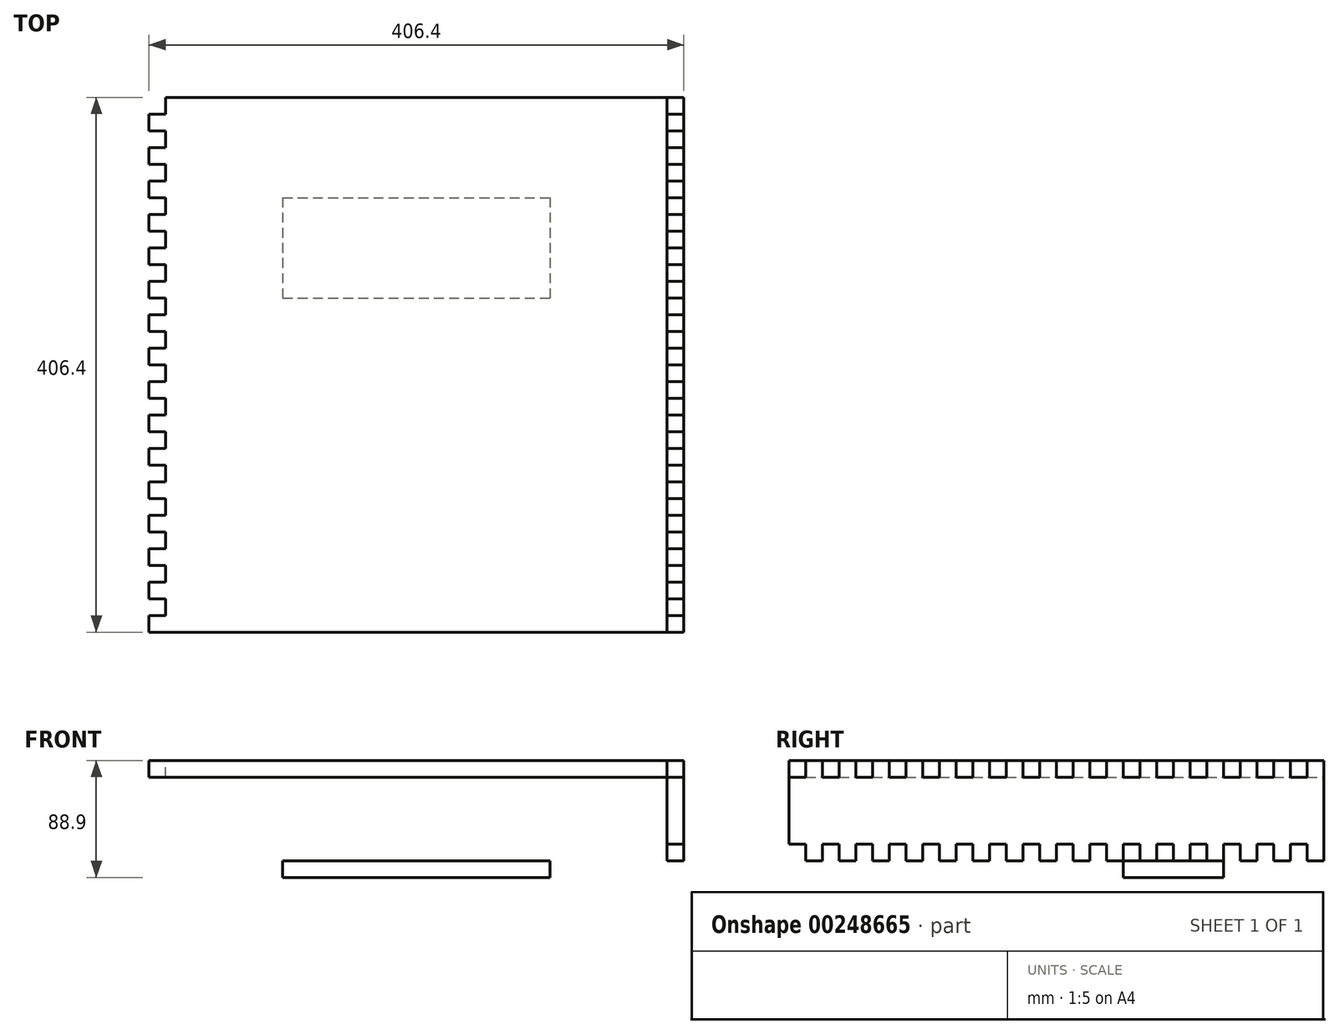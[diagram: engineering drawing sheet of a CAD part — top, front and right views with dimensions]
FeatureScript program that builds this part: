
annotation { "Feature Type Name" : "Feature", "Feature Type Description" : "" }
export const myFeature = defineFeature(function(context is Context, id is Id, definition is map)
    precondition{}
    {
        {
            var Q0;
            Q0=qCreatedBy(makeId("Top.planeOp"),FACE);
            var sketch = newSketch(context, id + "F0", { "sketchPlane" : qUnion([Q0])});
            skLineSegment(sketch, "E0.bottom", {"start": v(203.2, 203.2) * mm, "end": v(-203.2, 203.2) * mm});
            skLineSegment(sketch, "E0.top", {"start": v(203.2, -203.2) * mm, "end": v(-203.2, -203.2) * mm});
            skLineSegment(sketch, "E0.left", {"start": v(203.2, 203.2) * mm, "end": v(203.2, -203.2) * mm});
            skLineSegment(sketch, "E0.right", {"start": v(-203.2, 203.2) * mm, "end": v(-203.2, -203.2) * mm});
            skPoint(sketch, "E0.middle", {"position": v(0, 0) * mm});
            skSolve(sketch);
        }
        {
            var Q0;
            Q0 = qSketchRegion(id + "F0", true);
            extrude(context, id + "F1", {"entities" : qUnion([Q0]), "depth" : 12.7 * mm});
        }
        {
            var Q0;
            Q0=makeQuery(id+"F1.opExtrude","CAP_FACE",FACE,{"disambiguationData":[OSD([sQuery(id+"F0.wireOp",EDGE,"E0.bottom"),sQuery(id+"F0.wireOp",EDGE,"E0.top"),sQuery(id+"F0.wireOp",EDGE,"E0.left"),sQuery(id+"F0.wireOp",EDGE,"E0.right")])],"isStart":false});
            var sketch = newSketch(context, id + "F2", { "sketchPlane" : qUnion([Q0])});
            skLineSegment(sketch, "E1.bottom", {"start": v(-203.2, 203.2) * mm, "end": v(-190.5, 203.2) * mm});
            skLineSegment(sketch, "E1.top", {"start": v(-203.2, 190.5) * mm, "end": v(-190.5, 190.5) * mm});
            skLineSegment(sketch, "E1.left", {"start": v(-203.2, 203.2) * mm, "end": v(-203.2, 190.5) * mm});
            skLineSegment(sketch, "E1.right", {"start": v(-190.5, 203.2) * mm, "end": v(-190.5, 190.5) * mm});
            skLineSegment(sketch, "E2.0.1.0", {"start": v(-203.2, 177.8) * mm, "end": v(-203.2, 165.1) * mm});
            skLineSegment(sketch, "E2.0.1.1", {"start": v(-203.2, 165.1) * mm, "end": v(-190.5, 165.1) * mm});
            skLineSegment(sketch, "E2.0.1.2", {"start": v(-190.5, 177.8) * mm, "end": v(-190.5, 165.1) * mm});
            skLineSegment(sketch, "E2.0.1.3", {"start": v(-203.2, 177.8) * mm, "end": v(-190.5, 177.8) * mm});
            skLineSegment(sketch, "E2.0.2.0", {"start": v(-203.2, 152.4) * mm, "end": v(-203.2, 139.7) * mm});
            skLineSegment(sketch, "E2.0.2.1", {"start": v(-203.2, 139.7) * mm, "end": v(-190.5, 139.7) * mm});
            skLineSegment(sketch, "E2.0.2.2", {"start": v(-190.5, 152.4) * mm, "end": v(-190.5, 139.7) * mm});
            skLineSegment(sketch, "E2.0.2.3", {"start": v(-203.2, 152.4) * mm, "end": v(-190.5, 152.4) * mm});
            skLineSegment(sketch, "E2.0.3.0", {"start": v(-203.2, 127) * mm, "end": v(-203.2, 114.3) * mm});
            skLineSegment(sketch, "E2.0.3.1", {"start": v(-203.2, 114.3) * mm, "end": v(-190.5, 114.3) * mm});
            skLineSegment(sketch, "E2.0.3.2", {"start": v(-190.5, 127) * mm, "end": v(-190.5, 114.3) * mm});
            skLineSegment(sketch, "E2.0.3.3", {"start": v(-203.2, 127) * mm, "end": v(-190.5, 127) * mm});
            skLineSegment(sketch, "E2.0.4.0", {"start": v(-203.2, 101.6) * mm, "end": v(-203.2, 88.9) * mm});
            skLineSegment(sketch, "E2.0.4.1", {"start": v(-203.2, 88.9) * mm, "end": v(-190.5, 88.9) * mm});
            skLineSegment(sketch, "E2.0.4.2", {"start": v(-190.5, 101.6) * mm, "end": v(-190.5, 88.9) * mm});
            skLineSegment(sketch, "E2.0.4.3", {"start": v(-203.2, 101.6) * mm, "end": v(-190.5, 101.6) * mm});
            skLineSegment(sketch, "E2.0.5.0", {"start": v(-203.2, 76.2) * mm, "end": v(-203.2, 63.5) * mm});
            skLineSegment(sketch, "E2.0.5.1", {"start": v(-203.2, 63.5) * mm, "end": v(-190.5, 63.5) * mm});
            skLineSegment(sketch, "E2.0.5.2", {"start": v(-190.5, 76.2) * mm, "end": v(-190.5, 63.5) * mm});
            skLineSegment(sketch, "E2.0.5.3", {"start": v(-203.2, 76.2) * mm, "end": v(-190.5, 76.2) * mm});
            skLineSegment(sketch, "E2.0.6.0", {"start": v(-203.2, 50.8) * mm, "end": v(-203.2, 38.1) * mm});
            skLineSegment(sketch, "E2.0.6.1", {"start": v(-203.2, 38.1) * mm, "end": v(-190.5, 38.1) * mm});
            skLineSegment(sketch, "E2.0.6.2", {"start": v(-190.5, 50.8) * mm, "end": v(-190.5, 38.1) * mm});
            skLineSegment(sketch, "E2.0.6.3", {"start": v(-203.2, 50.8) * mm, "end": v(-190.5, 50.8) * mm});
            skLineSegment(sketch, "E2.0.7.0", {"start": v(-203.2, 25.4) * mm, "end": v(-203.2, 12.7) * mm});
            skLineSegment(sketch, "E2.0.7.1", {"start": v(-203.2, 12.7) * mm, "end": v(-190.5, 12.7) * mm});
            skLineSegment(sketch, "E2.0.7.2", {"start": v(-190.5, 25.4) * mm, "end": v(-190.5, 12.7) * mm});
            skLineSegment(sketch, "E2.0.7.3", {"start": v(-203.2, 25.4) * mm, "end": v(-190.5, 25.4) * mm});
            skLineSegment(sketch, "E2.0.8.0", {"start": v(-203.2, 0) * mm, "end": v(-203.2, -12.7) * mm});
            skLineSegment(sketch, "E2.0.8.1", {"start": v(-203.2, -12.7) * mm, "end": v(-190.5, -12.7) * mm});
            skLineSegment(sketch, "E2.0.8.2", {"start": v(-190.5, 0) * mm, "end": v(-190.5, -12.7) * mm});
            skLineSegment(sketch, "E2.0.8.3", {"start": v(-203.2, 0) * mm, "end": v(-190.5, 0) * mm});
            skLineSegment(sketch, "E2.0.9.0", {"start": v(-203.2, -25.4) * mm, "end": v(-203.2, -38.1) * mm});
            skLineSegment(sketch, "E2.0.9.1", {"start": v(-203.2, -38.1) * mm, "end": v(-190.5, -38.1) * mm});
            skLineSegment(sketch, "E2.0.9.2", {"start": v(-190.5, -25.4) * mm, "end": v(-190.5, -38.1) * mm});
            skLineSegment(sketch, "E2.0.9.3", {"start": v(-203.2, -25.4) * mm, "end": v(-190.5, -25.4) * mm});
            skLineSegment(sketch, "E2.0.10.0", {"start": v(-203.2, -50.8) * mm, "end": v(-203.2, -63.5) * mm});
            skLineSegment(sketch, "E2.0.10.1", {"start": v(-203.2, -63.5) * mm, "end": v(-190.5, -63.5) * mm});
            skLineSegment(sketch, "E2.0.10.2", {"start": v(-190.5, -50.8) * mm, "end": v(-190.5, -63.5) * mm});
            skLineSegment(sketch, "E2.0.10.3", {"start": v(-203.2, -50.8) * mm, "end": v(-190.5, -50.8) * mm});
            skLineSegment(sketch, "E2.0.11.0", {"start": v(-203.2, -76.2) * mm, "end": v(-203.2, -88.9) * mm});
            skLineSegment(sketch, "E2.0.11.1", {"start": v(-203.2, -88.9) * mm, "end": v(-190.5, -88.9) * mm});
            skLineSegment(sketch, "E2.0.11.2", {"start": v(-190.5, -76.2) * mm, "end": v(-190.5, -88.9) * mm});
            skLineSegment(sketch, "E2.0.11.3", {"start": v(-203.2, -76.2) * mm, "end": v(-190.5, -76.2) * mm});
            skLineSegment(sketch, "E2.0.12.0", {"start": v(-203.2, -101.6) * mm, "end": v(-203.2, -114.3) * mm});
            skLineSegment(sketch, "E2.0.12.1", {"start": v(-203.2, -114.3) * mm, "end": v(-190.5, -114.3) * mm});
            skLineSegment(sketch, "E2.0.12.2", {"start": v(-190.5, -101.6) * mm, "end": v(-190.5, -114.3) * mm});
            skLineSegment(sketch, "E2.0.12.3", {"start": v(-203.2, -101.6) * mm, "end": v(-190.5, -101.6) * mm});
            skLineSegment(sketch, "E2.0.13.0", {"start": v(-203.2, -127) * mm, "end": v(-203.2, -139.7) * mm});
            skLineSegment(sketch, "E2.0.13.1", {"start": v(-203.2, -139.7) * mm, "end": v(-190.5, -139.7) * mm});
            skLineSegment(sketch, "E2.0.13.2", {"start": v(-190.5, -127) * mm, "end": v(-190.5, -139.7) * mm});
            skLineSegment(sketch, "E2.0.13.3", {"start": v(-203.2, -127) * mm, "end": v(-190.5, -127) * mm});
            skLineSegment(sketch, "E2.0.14.0", {"start": v(-203.2, -152.4) * mm, "end": v(-203.2, -165.1) * mm});
            skLineSegment(sketch, "E2.0.14.1", {"start": v(-203.2, -165.1) * mm, "end": v(-190.5, -165.1) * mm});
            skLineSegment(sketch, "E2.0.14.2", {"start": v(-190.5, -152.4) * mm, "end": v(-190.5, -165.1) * mm});
            skLineSegment(sketch, "E2.0.14.3", {"start": v(-203.2, -152.4) * mm, "end": v(-190.5, -152.4) * mm});
            skLineSegment(sketch, "E2.0.15.0", {"start": v(-203.2, -177.8) * mm, "end": v(-203.2, -190.5) * mm});
            skLineSegment(sketch, "E2.0.15.1", {"start": v(-203.2, -190.5) * mm, "end": v(-190.5, -190.5) * mm});
            skLineSegment(sketch, "E2.0.15.2", {"start": v(-190.5, -177.8) * mm, "end": v(-190.5, -190.5) * mm});
            skLineSegment(sketch, "E2.0.15.3", {"start": v(-203.2, -177.8) * mm, "end": v(-190.5, -177.8) * mm});
            skLineSegment(sketch, "E2.direction1", {"start": v(-203.2, 190.5) * mm, "end": v(190.5, 190.5) * mm, "construction": true});
            skLineSegment(sketch, "E2.direction2", {"start": v(-203.2, 190.5) * mm, "end": v(-203.2, 165.1) * mm, "construction": true});
            skLineSegment(sketch, "E3.0.1.0", {"start": v(190.5, 203.2) * mm, "end": v(190.5, 190.5) * mm});
            skLineSegment(sketch, "E3.3.1.0", {"start": v(190.5, 190.5) * mm, "end": v(203.2, 190.5) * mm});
            skLineSegment(sketch, "E3.6.1.0", {"start": v(203.2, 203.2) * mm, "end": v(203.2, 190.5) * mm});
            skLineSegment(sketch, "E3.9.1.0", {"start": v(190.5, 203.2) * mm, "end": v(203.2, 203.2) * mm});
            skLineSegment(sketch, "E3.0.1.1", {"start": v(190.5, 177.8) * mm, "end": v(190.5, 165.1) * mm});
            skLineSegment(sketch, "E3.3.1.1", {"start": v(190.5, 165.1) * mm, "end": v(203.2, 165.1) * mm});
            skLineSegment(sketch, "E3.6.1.1", {"start": v(203.2, 177.8) * mm, "end": v(203.2, 165.1) * mm});
            skLineSegment(sketch, "E3.9.1.1", {"start": v(190.5, 177.8) * mm, "end": v(203.2, 177.8) * mm});
            skLineSegment(sketch, "E3.0.1.2", {"start": v(190.5, 152.4) * mm, "end": v(190.5, 139.7) * mm});
            skLineSegment(sketch, "E3.3.1.2", {"start": v(190.5, 139.7) * mm, "end": v(203.2, 139.7) * mm});
            skLineSegment(sketch, "E3.6.1.2", {"start": v(203.2, 152.4) * mm, "end": v(203.2, 139.7) * mm});
            skLineSegment(sketch, "E3.9.1.2", {"start": v(190.5, 152.4) * mm, "end": v(203.2, 152.4) * mm});
            skLineSegment(sketch, "E3.0.1.3", {"start": v(190.5, 127) * mm, "end": v(190.5, 114.3) * mm});
            skLineSegment(sketch, "E3.3.1.3", {"start": v(190.5, 114.3) * mm, "end": v(203.2, 114.3) * mm});
            skLineSegment(sketch, "E3.6.1.3", {"start": v(203.2, 127) * mm, "end": v(203.2, 114.3) * mm});
            skLineSegment(sketch, "E3.9.1.3", {"start": v(190.5, 127) * mm, "end": v(203.2, 127) * mm});
            skLineSegment(sketch, "E3.0.1.4", {"start": v(190.5, 101.6) * mm, "end": v(190.5, 88.9) * mm});
            skLineSegment(sketch, "E3.3.1.4", {"start": v(190.5, 88.9) * mm, "end": v(203.2, 88.9) * mm});
            skLineSegment(sketch, "E3.6.1.4", {"start": v(203.2, 101.6) * mm, "end": v(203.2, 88.9) * mm});
            skLineSegment(sketch, "E3.9.1.4", {"start": v(190.5, 101.6) * mm, "end": v(203.2, 101.6) * mm});
            skLineSegment(sketch, "E3.0.1.5", {"start": v(190.5, 76.2) * mm, "end": v(190.5, 63.5) * mm});
            skLineSegment(sketch, "E3.3.1.5", {"start": v(190.5, 63.5) * mm, "end": v(203.2, 63.5) * mm});
            skLineSegment(sketch, "E3.6.1.5", {"start": v(203.2, 76.2) * mm, "end": v(203.2, 63.5) * mm});
            skLineSegment(sketch, "E3.9.1.5", {"start": v(190.5, 76.2) * mm, "end": v(203.2, 76.2) * mm});
            skLineSegment(sketch, "E3.0.1.6", {"start": v(190.5, 50.8) * mm, "end": v(190.5, 38.1) * mm});
            skLineSegment(sketch, "E3.3.1.6", {"start": v(190.5, 38.1) * mm, "end": v(203.2, 38.1) * mm});
            skLineSegment(sketch, "E3.6.1.6", {"start": v(203.2, 50.8) * mm, "end": v(203.2, 38.1) * mm});
            skLineSegment(sketch, "E3.9.1.6", {"start": v(190.5, 50.8) * mm, "end": v(203.2, 50.8) * mm});
            skLineSegment(sketch, "E3.0.1.7", {"start": v(190.5, 25.4) * mm, "end": v(190.5, 12.7) * mm});
            skLineSegment(sketch, "E3.3.1.7", {"start": v(190.5, 12.7) * mm, "end": v(203.2, 12.7) * mm});
            skLineSegment(sketch, "E3.6.1.7", {"start": v(203.2, 25.4) * mm, "end": v(203.2, 12.7) * mm});
            skLineSegment(sketch, "E3.9.1.7", {"start": v(190.5, 25.4) * mm, "end": v(203.2, 25.4) * mm});
            skLineSegment(sketch, "E3.0.1.8", {"start": v(190.5, 0) * mm, "end": v(190.5, -12.7) * mm});
            skLineSegment(sketch, "E3.3.1.8", {"start": v(190.5, -12.7) * mm, "end": v(203.2, -12.7) * mm});
            skLineSegment(sketch, "E3.6.1.8", {"start": v(203.2, 0) * mm, "end": v(203.2, -12.7) * mm});
            skLineSegment(sketch, "E3.9.1.8", {"start": v(190.5, 0) * mm, "end": v(203.2, 0) * mm});
            skLineSegment(sketch, "E3.0.1.9", {"start": v(190.5, -25.4) * mm, "end": v(190.5, -38.1) * mm});
            skLineSegment(sketch, "E3.3.1.9", {"start": v(190.5, -38.1) * mm, "end": v(203.2, -38.1) * mm});
            skLineSegment(sketch, "E3.6.1.9", {"start": v(203.2, -25.4) * mm, "end": v(203.2, -38.1) * mm});
            skLineSegment(sketch, "E3.9.1.9", {"start": v(190.5, -25.4) * mm, "end": v(203.2, -25.4) * mm});
            skLineSegment(sketch, "E3.0.1.10", {"start": v(190.5, -50.8) * mm, "end": v(190.5, -63.5) * mm});
            skLineSegment(sketch, "E3.3.1.10", {"start": v(190.5, -63.5) * mm, "end": v(203.2, -63.5) * mm});
            skLineSegment(sketch, "E3.6.1.10", {"start": v(203.2, -50.8) * mm, "end": v(203.2, -63.5) * mm});
            skLineSegment(sketch, "E3.9.1.10", {"start": v(190.5, -50.8) * mm, "end": v(203.2, -50.8) * mm});
            skLineSegment(sketch, "E3.0.1.11", {"start": v(190.5, -76.2) * mm, "end": v(190.5, -88.9) * mm});
            skLineSegment(sketch, "E3.3.1.11", {"start": v(190.5, -88.9) * mm, "end": v(203.2, -88.9) * mm});
            skLineSegment(sketch, "E3.6.1.11", {"start": v(203.2, -76.2) * mm, "end": v(203.2, -88.9) * mm});
            skLineSegment(sketch, "E3.9.1.11", {"start": v(190.5, -76.2) * mm, "end": v(203.2, -76.2) * mm});
            skLineSegment(sketch, "E3.0.1.12", {"start": v(190.5, -101.6) * mm, "end": v(190.5, -114.3) * mm});
            skLineSegment(sketch, "E3.3.1.12", {"start": v(190.5, -114.3) * mm, "end": v(203.2, -114.3) * mm});
            skLineSegment(sketch, "E3.6.1.12", {"start": v(203.2, -101.6) * mm, "end": v(203.2, -114.3) * mm});
            skLineSegment(sketch, "E3.9.1.12", {"start": v(190.5, -101.6) * mm, "end": v(203.2, -101.6) * mm});
            skLineSegment(sketch, "E3.0.1.13", {"start": v(190.5, -127) * mm, "end": v(190.5, -139.7) * mm});
            skLineSegment(sketch, "E3.3.1.13", {"start": v(190.5, -139.7) * mm, "end": v(203.2, -139.7) * mm});
            skLineSegment(sketch, "E3.6.1.13", {"start": v(203.2, -127) * mm, "end": v(203.2, -139.7) * mm});
            skLineSegment(sketch, "E3.9.1.13", {"start": v(190.5, -127) * mm, "end": v(203.2, -127) * mm});
            skLineSegment(sketch, "E3.0.1.14", {"start": v(190.5, -152.4) * mm, "end": v(190.5, -165.1) * mm});
            skLineSegment(sketch, "E3.3.1.14", {"start": v(190.5, -165.1) * mm, "end": v(203.2, -165.1) * mm});
            skLineSegment(sketch, "E3.6.1.14", {"start": v(203.2, -152.4) * mm, "end": v(203.2, -165.1) * mm});
            skLineSegment(sketch, "E3.9.1.14", {"start": v(190.5, -152.4) * mm, "end": v(203.2, -152.4) * mm});
            skLineSegment(sketch, "E3.0.1.15", {"start": v(190.5, -177.8) * mm, "end": v(190.5, -190.5) * mm});
            skLineSegment(sketch, "E3.3.1.15", {"start": v(190.5, -190.5) * mm, "end": v(203.2, -190.5) * mm});
            skLineSegment(sketch, "E3.6.1.15", {"start": v(203.2, -177.8) * mm, "end": v(203.2, -190.5) * mm});
            skLineSegment(sketch, "E3.9.1.15", {"start": v(190.5, -177.8) * mm, "end": v(203.2, -177.8) * mm});
            skSolve(sketch);
        }
        {
            var Q0;
            Q0 = qSketchRegion(id + "F2", true);
            extrude(context, id + "F3", {"entities" : qUnion([Q0]), "operationType" : NewBodyOperationType.REMOVE, "endBound" : BoundingType.UP_TO_NEXT, "oppositeDirection" : true, "depth" : 25.4 * mm});
        }
        {
            var Q0;
            {var subQ1=sQuery(id+"F0.wireOp",EDGE,"E0.left");var subQ2=sQuery(id+"F0.wireOp",EDGE,"E0.top");Q0=makeQuery(id+"F3.boolean.opBoolean","SPLIT",FACE,{"disambiguationData":[TD([makeQuery(id+"F1.opExtrude","SWEPT_FACE",FACE,{"disambiguationData":[OSD([subQ2])]})])],"derivedFrom":makeQuery(id+"F1.opExtrude","SWEPT_FACE",FACE,{"disambiguationData":[OSD([subQ1])]})});}
            var sketch = newSketch(context, id + "F4", { "sketchPlane" : qUnion([Q0])});
            skLineSegment(sketch, "E4.bottom", {"start": v(-203.2, 12.7) * mm, "end": v(203.2, 12.7) * mm});
            skLineSegment(sketch, "E4.top", {"start": v(-203.2, -63.5) * mm, "end": v(203.2, -63.5) * mm});
            skLineSegment(sketch, "E4.left", {"start": v(-203.2, 12.7) * mm, "end": v(-203.2, -63.5) * mm});
            skLineSegment(sketch, "E4.right", {"start": v(203.2, 12.7) * mm, "end": v(203.2, -63.5) * mm});
            skSolve(sketch);
        }
        {
            var Q0;
            Q0 = qSketchRegion(id + "F4", true);
            extrude(context, id + "F5", {"entities" : qUnion([Q0]), "oppositeDirection" : true, "depth" : 12.7 * mm});
        }
        {
            var Q0;
            Q0=makeQuery(id+"F5.opExtrude","CAP_FACE",FACE,{"disambiguationData":[OSD([sQuery(id+"F4.wireOp",EDGE,"E4.bottom"),sQuery(id+"F4.wireOp",EDGE,"E4.top"),sQuery(id+"F4.wireOp",EDGE,"E4.left"),sQuery(id+"F4.wireOp",EDGE,"E4.right")])],"isStart":true});
            var sketch = newSketch(context, id + "F6", { "sketchPlane" : qUnion([Q0])});
            skLineSegment(sketch, "E5.0", {"start": v(-203.2, 12.7) * mm, "end": v(-190.5, 12.7) * mm});
            skLineSegment(sketch, "E5.1", {"start": v(-203.2, 12.7) * mm, "end": v(-203.2, 0) * mm});
            skLineSegment(sketch, "E5.2", {"start": v(-190.5, 0) * mm, "end": v(-190.5, 12.7) * mm});
            skLineSegment(sketch, "E5.3", {"start": v(-190.5, 0) * mm, "end": v(-203.2, 0) * mm});
            skPoint(sketch, "E6.orphan", {"position": v(203.2, 12.7) * mm});
            skPoint(sketch, "E7.orphan", {"position": v(-203.2, -63.5) * mm});
            skLineSegment(sketch, "E8.0.1.0", {"start": v(-203.2, -50.8) * mm, "end": v(-190.5, -50.8) * mm});
            skLineSegment(sketch, "E8.0.1.1", {"start": v(-190.5, -63.5) * mm, "end": v(-190.5, -50.8) * mm});
            skLineSegment(sketch, "E8.0.1.2", {"start": v(-190.5, -63.5) * mm, "end": v(-203.2, -63.5) * mm});
            skLineSegment(sketch, "E8.0.1.3", {"start": v(-203.2, -50.8) * mm, "end": v(-203.2, -63.5) * mm});
            skLineSegment(sketch, "E8.1.0.0", {"start": v(-177.8, 12.7) * mm, "end": v(-165.1, 12.7) * mm});
            skLineSegment(sketch, "E8.1.0.1", {"start": v(-165.1, 0) * mm, "end": v(-165.1, 12.7) * mm});
            skLineSegment(sketch, "E8.1.0.2", {"start": v(-165.1, 0) * mm, "end": v(-177.8, 0) * mm});
            skLineSegment(sketch, "E8.1.0.3", {"start": v(-177.8, 12.7) * mm, "end": v(-177.8, 0) * mm});
            skLineSegment(sketch, "E8.1.1.0", {"start": v(-177.8, -50.8) * mm, "end": v(-165.1, -50.8) * mm});
            skLineSegment(sketch, "E8.1.1.1", {"start": v(-165.1, -63.5) * mm, "end": v(-165.1, -50.8) * mm});
            skLineSegment(sketch, "E8.1.1.2", {"start": v(-165.1, -63.5) * mm, "end": v(-177.8, -63.5) * mm});
            skLineSegment(sketch, "E8.1.1.3", {"start": v(-177.8, -50.8) * mm, "end": v(-177.8, -63.5) * mm});
            skLineSegment(sketch, "E8.2.0.0", {"start": v(-152.4, 12.7) * mm, "end": v(-139.7, 12.7) * mm});
            skLineSegment(sketch, "E8.2.0.1", {"start": v(-139.7, 0) * mm, "end": v(-139.7, 12.7) * mm});
            skLineSegment(sketch, "E8.2.0.2", {"start": v(-139.7, 0) * mm, "end": v(-152.4, 0) * mm});
            skLineSegment(sketch, "E8.2.0.3", {"start": v(-152.4, 12.7) * mm, "end": v(-152.4, 0) * mm});
            skLineSegment(sketch, "E8.2.1.0", {"start": v(-152.4, -50.8) * mm, "end": v(-139.7, -50.8) * mm});
            skLineSegment(sketch, "E8.2.1.1", {"start": v(-139.7, -63.5) * mm, "end": v(-139.7, -50.8) * mm});
            skLineSegment(sketch, "E8.2.1.2", {"start": v(-139.7, -63.5) * mm, "end": v(-152.4, -63.5) * mm});
            skLineSegment(sketch, "E8.2.1.3", {"start": v(-152.4, -50.8) * mm, "end": v(-152.4, -63.5) * mm});
            skLineSegment(sketch, "E8.3.0.0", {"start": v(-127, 12.7) * mm, "end": v(-114.3, 12.7) * mm});
            skLineSegment(sketch, "E8.3.0.1", {"start": v(-114.3, 0) * mm, "end": v(-114.3, 12.7) * mm});
            skLineSegment(sketch, "E8.3.0.2", {"start": v(-114.3, 0) * mm, "end": v(-127, 0) * mm});
            skLineSegment(sketch, "E8.3.0.3", {"start": v(-127, 12.7) * mm, "end": v(-127, 0) * mm});
            skLineSegment(sketch, "E8.3.1.0", {"start": v(-127, -50.8) * mm, "end": v(-114.3, -50.8) * mm});
            skLineSegment(sketch, "E8.3.1.1", {"start": v(-114.3, -63.5) * mm, "end": v(-114.3, -50.8) * mm});
            skLineSegment(sketch, "E8.3.1.2", {"start": v(-114.3, -63.5) * mm, "end": v(-127, -63.5) * mm});
            skLineSegment(sketch, "E8.3.1.3", {"start": v(-127, -50.8) * mm, "end": v(-127, -63.5) * mm});
            skLineSegment(sketch, "E8.4.0.0", {"start": v(-101.6, 12.7) * mm, "end": v(-88.9, 12.7) * mm});
            skLineSegment(sketch, "E8.4.0.1", {"start": v(-88.9, 0) * mm, "end": v(-88.9, 12.7) * mm});
            skLineSegment(sketch, "E8.4.0.2", {"start": v(-88.9, 0) * mm, "end": v(-101.6, 0) * mm});
            skLineSegment(sketch, "E8.4.0.3", {"start": v(-101.6, 12.7) * mm, "end": v(-101.6, 0) * mm});
            skLineSegment(sketch, "E8.4.1.0", {"start": v(-101.6, -50.8) * mm, "end": v(-88.9, -50.8) * mm});
            skLineSegment(sketch, "E8.4.1.1", {"start": v(-88.9, -63.5) * mm, "end": v(-88.9, -50.8) * mm});
            skLineSegment(sketch, "E8.4.1.2", {"start": v(-88.9, -63.5) * mm, "end": v(-101.6, -63.5) * mm});
            skLineSegment(sketch, "E8.4.1.3", {"start": v(-101.6, -50.8) * mm, "end": v(-101.6, -63.5) * mm});
            skLineSegment(sketch, "E8.5.0.0", {"start": v(-76.2, 12.7) * mm, "end": v(-63.5, 12.7) * mm});
            skLineSegment(sketch, "E8.5.0.1", {"start": v(-63.5, 0) * mm, "end": v(-63.5, 12.7) * mm});
            skLineSegment(sketch, "E8.5.0.2", {"start": v(-63.5, 0) * mm, "end": v(-76.2, 0) * mm});
            skLineSegment(sketch, "E8.5.0.3", {"start": v(-76.2, 12.7) * mm, "end": v(-76.2, 0) * mm});
            skLineSegment(sketch, "E8.5.1.0", {"start": v(-76.2, -50.8) * mm, "end": v(-63.5, -50.8) * mm});
            skLineSegment(sketch, "E8.5.1.1", {"start": v(-63.5, -63.5) * mm, "end": v(-63.5, -50.8) * mm});
            skLineSegment(sketch, "E8.5.1.2", {"start": v(-63.5, -63.5) * mm, "end": v(-76.2, -63.5) * mm});
            skLineSegment(sketch, "E8.5.1.3", {"start": v(-76.2, -50.8) * mm, "end": v(-76.2, -63.5) * mm});
            skLineSegment(sketch, "E8.6.0.0", {"start": v(-50.8, 12.7) * mm, "end": v(-38.1, 12.7) * mm});
            skLineSegment(sketch, "E8.6.0.1", {"start": v(-38.1, 0) * mm, "end": v(-38.1, 12.7) * mm});
            skLineSegment(sketch, "E8.6.0.2", {"start": v(-38.1, 0) * mm, "end": v(-50.8, 0) * mm});
            skLineSegment(sketch, "E8.6.0.3", {"start": v(-50.8, 12.7) * mm, "end": v(-50.8, 0) * mm});
            skLineSegment(sketch, "E8.6.1.0", {"start": v(-50.8, -50.8) * mm, "end": v(-38.1, -50.8) * mm});
            skLineSegment(sketch, "E8.6.1.1", {"start": v(-38.1, -63.5) * mm, "end": v(-38.1, -50.8) * mm});
            skLineSegment(sketch, "E8.6.1.2", {"start": v(-38.1, -63.5) * mm, "end": v(-50.8, -63.5) * mm});
            skLineSegment(sketch, "E8.6.1.3", {"start": v(-50.8, -50.8) * mm, "end": v(-50.8, -63.5) * mm});
            skLineSegment(sketch, "E8.7.0.0", {"start": v(-25.4, 12.7) * mm, "end": v(-12.7, 12.7) * mm});
            skLineSegment(sketch, "E8.7.0.1", {"start": v(-12.7, 0) * mm, "end": v(-12.7, 12.7) * mm});
            skLineSegment(sketch, "E8.7.0.2", {"start": v(-12.7, 0) * mm, "end": v(-25.4, 0) * mm});
            skLineSegment(sketch, "E8.7.0.3", {"start": v(-25.4, 12.7) * mm, "end": v(-25.4, 0) * mm});
            skLineSegment(sketch, "E8.7.1.0", {"start": v(-25.4, -50.8) * mm, "end": v(-12.7, -50.8) * mm});
            skLineSegment(sketch, "E8.7.1.1", {"start": v(-12.7, -63.5) * mm, "end": v(-12.7, -50.8) * mm});
            skLineSegment(sketch, "E8.7.1.2", {"start": v(-12.7, -63.5) * mm, "end": v(-25.4, -63.5) * mm});
            skLineSegment(sketch, "E8.7.1.3", {"start": v(-25.4, -50.8) * mm, "end": v(-25.4, -63.5) * mm});
            skLineSegment(sketch, "E8.8.0.0", {"start": v(0, 12.7) * mm, "end": v(12.7, 12.7) * mm});
            skLineSegment(sketch, "E8.8.0.1", {"start": v(12.7, 0) * mm, "end": v(12.7, 12.7) * mm});
            skLineSegment(sketch, "E8.8.0.2", {"start": v(12.7, 0) * mm, "end": v(0, 0) * mm});
            skLineSegment(sketch, "E8.8.0.3", {"start": v(0, 12.7) * mm, "end": v(0, 0) * mm});
            skLineSegment(sketch, "E8.8.1.0", {"start": v(0, -50.8) * mm, "end": v(12.7, -50.8) * mm});
            skLineSegment(sketch, "E8.8.1.1", {"start": v(12.7, -63.5) * mm, "end": v(12.7, -50.8) * mm});
            skLineSegment(sketch, "E8.8.1.2", {"start": v(12.7, -63.5) * mm, "end": v(0, -63.5) * mm});
            skLineSegment(sketch, "E8.8.1.3", {"start": v(0, -50.8) * mm, "end": v(0, -63.5) * mm});
            skLineSegment(sketch, "E8.9.0.0", {"start": v(25.4, 12.7) * mm, "end": v(38.1, 12.7) * mm});
            skLineSegment(sketch, "E8.9.0.1", {"start": v(38.1, 0) * mm, "end": v(38.1, 12.7) * mm});
            skLineSegment(sketch, "E8.9.0.2", {"start": v(38.1, 0) * mm, "end": v(25.4, 0) * mm});
            skLineSegment(sketch, "E8.9.0.3", {"start": v(25.4, 12.7) * mm, "end": v(25.4, 0) * mm});
            skLineSegment(sketch, "E8.9.1.0", {"start": v(25.4, -50.8) * mm, "end": v(38.1, -50.8) * mm});
            skLineSegment(sketch, "E8.9.1.1", {"start": v(38.1, -63.5) * mm, "end": v(38.1, -50.8) * mm});
            skLineSegment(sketch, "E8.9.1.2", {"start": v(38.1, -63.5) * mm, "end": v(25.4, -63.5) * mm});
            skLineSegment(sketch, "E8.9.1.3", {"start": v(25.4, -50.8) * mm, "end": v(25.4, -63.5) * mm});
            skLineSegment(sketch, "E8.10.0.0", {"start": v(50.8, 12.7) * mm, "end": v(63.5, 12.7) * mm});
            skLineSegment(sketch, "E8.10.0.1", {"start": v(63.5, 0) * mm, "end": v(63.5, 12.7) * mm});
            skLineSegment(sketch, "E8.10.0.2", {"start": v(63.5, 0) * mm, "end": v(50.8, 0) * mm});
            skLineSegment(sketch, "E8.10.0.3", {"start": v(50.8, 12.7) * mm, "end": v(50.8, 0) * mm});
            skLineSegment(sketch, "E8.10.1.0", {"start": v(50.8, -50.8) * mm, "end": v(63.5, -50.8) * mm});
            skLineSegment(sketch, "E8.10.1.1", {"start": v(63.5, -63.5) * mm, "end": v(63.5, -50.8) * mm});
            skLineSegment(sketch, "E8.10.1.2", {"start": v(63.5, -63.5) * mm, "end": v(50.8, -63.5) * mm});
            skLineSegment(sketch, "E8.10.1.3", {"start": v(50.8, -50.8) * mm, "end": v(50.8, -63.5) * mm});
            skLineSegment(sketch, "E8.11.0.0", {"start": v(76.2, 12.7) * mm, "end": v(88.9, 12.7) * mm});
            skLineSegment(sketch, "E8.11.0.1", {"start": v(88.9, 0) * mm, "end": v(88.9, 12.7) * mm});
            skLineSegment(sketch, "E8.11.0.2", {"start": v(88.9, 0) * mm, "end": v(76.2, 0) * mm});
            skLineSegment(sketch, "E8.11.0.3", {"start": v(76.2, 12.7) * mm, "end": v(76.2, 0) * mm});
            skLineSegment(sketch, "E8.11.1.0", {"start": v(76.2, -50.8) * mm, "end": v(88.9, -50.8) * mm});
            skLineSegment(sketch, "E8.11.1.1", {"start": v(88.9, -63.5) * mm, "end": v(88.9, -50.8) * mm});
            skLineSegment(sketch, "E8.11.1.2", {"start": v(88.9, -63.5) * mm, "end": v(76.2, -63.5) * mm});
            skLineSegment(sketch, "E8.11.1.3", {"start": v(76.2, -50.8) * mm, "end": v(76.2, -63.5) * mm});
            skLineSegment(sketch, "E8.12.0.0", {"start": v(101.6, 12.7) * mm, "end": v(114.3, 12.7) * mm});
            skLineSegment(sketch, "E8.12.0.1", {"start": v(114.3, 0) * mm, "end": v(114.3, 12.7) * mm});
            skLineSegment(sketch, "E8.12.0.2", {"start": v(114.3, 0) * mm, "end": v(101.6, 0) * mm});
            skLineSegment(sketch, "E8.12.0.3", {"start": v(101.6, 12.7) * mm, "end": v(101.6, 0) * mm});
            skLineSegment(sketch, "E8.12.1.0", {"start": v(101.6, -50.8) * mm, "end": v(114.3, -50.8) * mm});
            skLineSegment(sketch, "E8.12.1.1", {"start": v(114.3, -63.5) * mm, "end": v(114.3, -50.8) * mm});
            skLineSegment(sketch, "E8.12.1.2", {"start": v(114.3, -63.5) * mm, "end": v(101.6, -63.5) * mm});
            skLineSegment(sketch, "E8.12.1.3", {"start": v(101.6, -50.8) * mm, "end": v(101.6, -63.5) * mm});
            skLineSegment(sketch, "E8.13.0.0", {"start": v(127, 12.7) * mm, "end": v(139.7, 12.7) * mm});
            skLineSegment(sketch, "E8.13.0.1", {"start": v(139.7, 0) * mm, "end": v(139.7, 12.7) * mm});
            skLineSegment(sketch, "E8.13.0.2", {"start": v(139.7, 0) * mm, "end": v(127, 0) * mm});
            skLineSegment(sketch, "E8.13.0.3", {"start": v(127, 12.7) * mm, "end": v(127, 0) * mm});
            skLineSegment(sketch, "E8.13.1.0", {"start": v(127, -50.8) * mm, "end": v(139.7, -50.8) * mm});
            skLineSegment(sketch, "E8.13.1.1", {"start": v(139.7, -63.5) * mm, "end": v(139.7, -50.8) * mm});
            skLineSegment(sketch, "E8.13.1.2", {"start": v(139.7, -63.5) * mm, "end": v(127, -63.5) * mm});
            skLineSegment(sketch, "E8.13.1.3", {"start": v(127, -50.8) * mm, "end": v(127, -63.5) * mm});
            skLineSegment(sketch, "E8.14.0.0", {"start": v(152.4, 12.7) * mm, "end": v(165.1, 12.7) * mm});
            skLineSegment(sketch, "E8.14.0.1", {"start": v(165.1, 0) * mm, "end": v(165.1, 12.7) * mm});
            skLineSegment(sketch, "E8.14.0.2", {"start": v(165.1, 0) * mm, "end": v(152.4, 0) * mm});
            skLineSegment(sketch, "E8.14.0.3", {"start": v(152.4, 12.7) * mm, "end": v(152.4, 0) * mm});
            skLineSegment(sketch, "E8.14.1.0", {"start": v(152.4, -50.8) * mm, "end": v(165.1, -50.8) * mm});
            skLineSegment(sketch, "E8.14.1.1", {"start": v(165.1, -63.5) * mm, "end": v(165.1, -50.8) * mm});
            skLineSegment(sketch, "E8.14.1.2", {"start": v(165.1, -63.5) * mm, "end": v(152.4, -63.5) * mm});
            skLineSegment(sketch, "E8.14.1.3", {"start": v(152.4, -50.8) * mm, "end": v(152.4, -63.5) * mm});
            skLineSegment(sketch, "E8.15.0.0", {"start": v(177.8, 12.7) * mm, "end": v(190.5, 12.7) * mm});
            skLineSegment(sketch, "E8.15.0.1", {"start": v(190.5, 0) * mm, "end": v(190.5, 12.7) * mm});
            skLineSegment(sketch, "E8.15.0.2", {"start": v(190.5, 0) * mm, "end": v(177.8, 0) * mm});
            skLineSegment(sketch, "E8.15.0.3", {"start": v(177.8, 12.7) * mm, "end": v(177.8, 0) * mm});
            skLineSegment(sketch, "E8.15.1.0", {"start": v(177.8, -50.8) * mm, "end": v(190.5, -50.8) * mm});
            skLineSegment(sketch, "E8.15.1.1", {"start": v(190.5, -63.5) * mm, "end": v(190.5, -50.8) * mm});
            skLineSegment(sketch, "E8.15.1.2", {"start": v(190.5, -63.5) * mm, "end": v(177.8, -63.5) * mm});
            skLineSegment(sketch, "E8.15.1.3", {"start": v(177.8, -50.8) * mm, "end": v(177.8, -63.5) * mm});
            skLineSegment(sketch, "E8.direction1", {"start": v(-203.2, 12.7) * mm, "end": v(-177.8, 12.7) * mm, "construction": true});
            skLineSegment(sketch, "E8.direction2", {"start": v(-203.2, 12.7) * mm, "end": v(-203.2, -50.8) * mm, "construction": true});
            skSolve(sketch);
        }
        {
            var Q0;
            Q0 = qSketchRegion(id + "F6", true);
            extrude(context, id + "F7", {"entities" : qUnion([Q0]), "operationType" : NewBodyOperationType.REMOVE, "endBound" : BoundingType.UP_TO_NEXT, "oppositeDirection" : true, "depth" : 25.4 * mm});
        }
        {
            var Q0;
            {var subQ2=sQuery(id+"F4.wireOp",EDGE,"E4.top");Q0=makeQuery(id+"F7.boolean.opBoolean","SPLIT",FACE,{"disambiguationData":[TD([makeQuery(id+"F7.opExtrude","SWEPT_FACE",FACE,{"disambiguationData":[OSD([sQuery(id+"F6.wireOp",EDGE,"E8.7.1.1")])]})])],"derivedFrom":makeQuery(id+"F5.opExtrude","SWEPT_FACE",FACE,{"disambiguationData":[OSD([subQ2])]})});}
            var sketch = newSketch(context, id + "F8", { "sketchPlane" : qUnion([Q0])});
            skLineSegment(sketch, "E9.bottom", {"start": v(-101.6, -127) * mm, "end": v(101.6, -127) * mm});
            skLineSegment(sketch, "E9.top", {"start": v(-101.6, -50.8) * mm, "end": v(101.6, -50.8) * mm});
            skLineSegment(sketch, "E9.left", {"start": v(-101.6, -127) * mm, "end": v(-101.6, -50.8) * mm});
            skLineSegment(sketch, "E9.right", {"start": v(101.6, -127) * mm, "end": v(101.6, -50.8) * mm});
            skLineSegment(sketch, "E10.0", {"start": v(203.2, 203.2) * mm, "end": v(-203.2, 203.2) * mm, "construction": true});
            skLineSegment(sketch, "E11", {"start": v(0, 203.2) * mm, "end": v(0, -50.8) * mm, "construction": true});
            skSolve(sketch);
        }
        {
            var Q0;
            Q0 = qSketchRegion(id + "F8", true);
            extrude(context, id + "F9", {"entities" : qUnion([Q0]), "depth" : 12.7 * mm});
        }
    });
